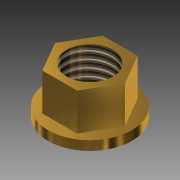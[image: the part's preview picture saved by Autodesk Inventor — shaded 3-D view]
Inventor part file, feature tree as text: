
AUTODESK INVENTOR PART (.ipt)
format: ipt  version: 2015 (Build 190159000, 159)  size: 104,960 bytes
history: native  units: mm
features: extrude x3, sketch x3, thread x1
ambient origin geometry x8: Origin, YZ Plane, XZ Plane, XY Plane, X Axis, Y Axis, Z Axis, Center Point
bodies: 实体1 (feature_tree)
feature tree (7):
  extrude  "拉伸1"  Depth=1.0mm TaperAngle=0.0deg
  extrude  "拉伸2"  Depth=4.0mm TaperAngle=0.0deg
  extrude  "拉伸3"  Depth=4.0mm TaperAngle=0.0deg
  thread  "螺纹1"  [1 undecoded]
  sketch  "草图1"  dims[d0=9.0mm d1=1.0mm d2=0.0mm]
  sketch  "草图2"  dims[d3=6.5mm d4=4.0mm d5=0.0mm]
  sketch  "草图3"  dims[d6=5.0mm d7=4.0mm d8=0.0mm d9=10.0mm d10=0.0mm]
note: 1 required parameter value undecoded (feature->parameter linkage not recoverable at this tier; creation-order binding heuristic only, values carry confidence <= 0.55)
